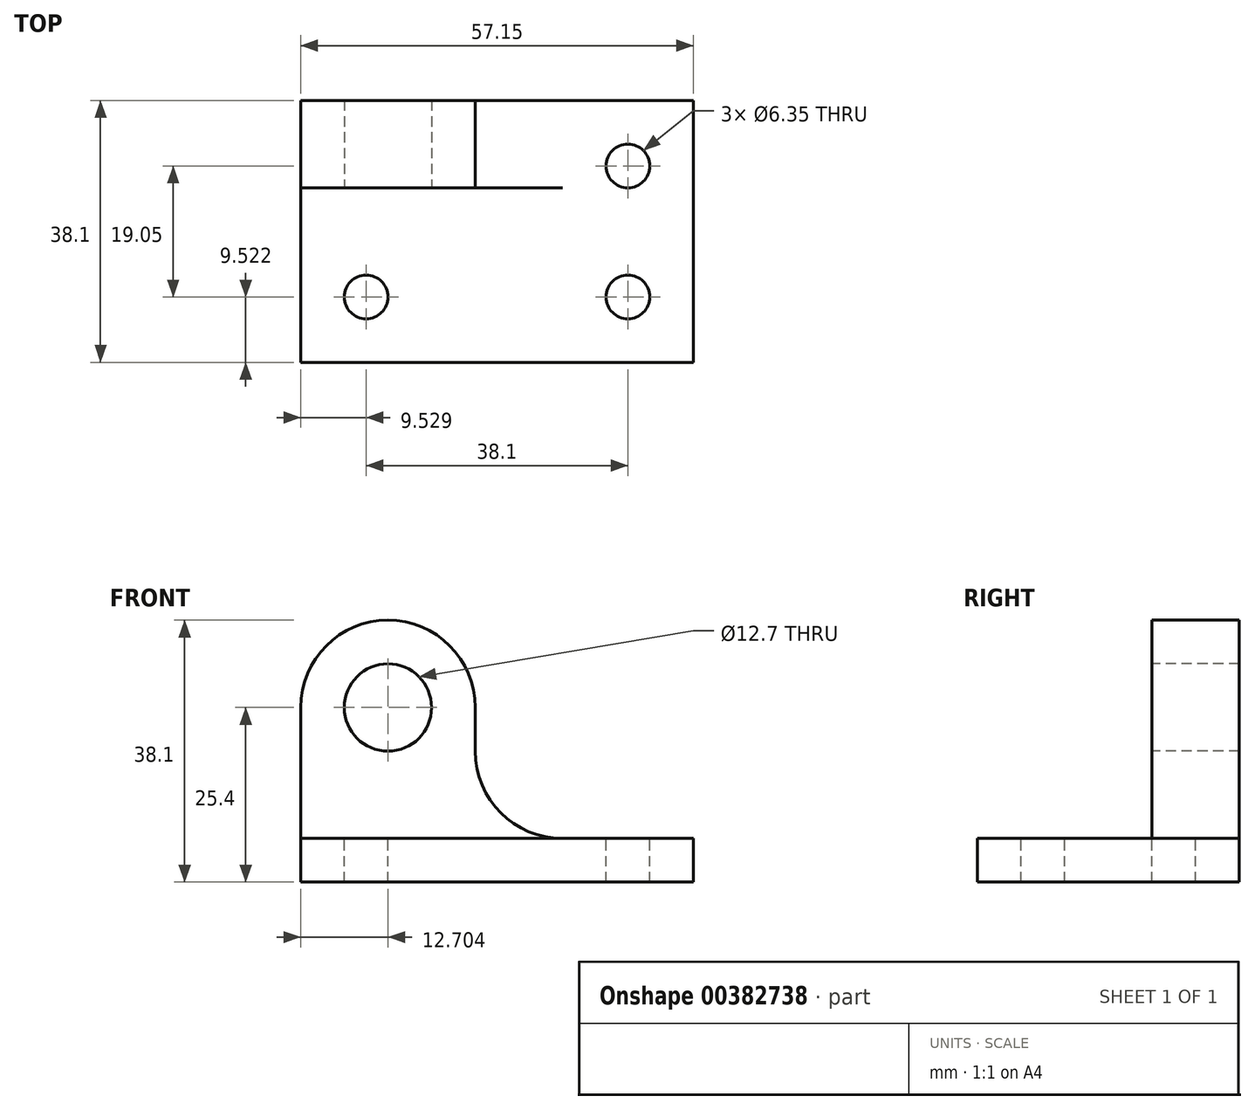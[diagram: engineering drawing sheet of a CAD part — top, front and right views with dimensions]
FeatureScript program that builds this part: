
annotation { "Feature Type Name" : "Feature", "Feature Type Description" : "" }
export const myFeature = defineFeature(function(context is Context, id is Id, definition is map)
    precondition{}
    {
        {
            var Q0;
            Q0=qCreatedBy(makeId("Top.planeOp"),FACE);
            var sketch = newSketch(context, id + "F0", { "sketchPlane" : qUnion([Q0])});
            skLineSegment(sketch, "E0.bottom", {"start": v(-24.7, -21.01) * mm, "end": v(32.44, -21.01) * mm});
            skLineSegment(sketch, "E0.top", {"start": v(-24.7, 17.09) * mm, "end": v(32.44, 17.09) * mm});
            skLineSegment(sketch, "E0.left", {"start": v(-24.7, -21.01) * mm, "end": v(-24.7, 17.09) * mm});
            skLineSegment(sketch, "E0.right", {"start": v(32.44, -21.01) * mm, "end": v(32.44, 17.09) * mm});
            skSolve(sketch);
        }
        {
            var Q0;
            Q0 = qSketchRegion(id + "F0", true);
            extrude(context, id + "F1", {"entities" : qUnion([Q0]), "depth" : 6.35 * mm});
        }
        {
            var Q0;
            Q0=makeQuery(id+"F1.opExtrude","CAP_FACE",FACE,{"disambiguationData":[OSD([sQuery(id+"F0.wireOp",EDGE,"E0.bottom"),sQuery(id+"F0.wireOp",EDGE,"E0.top"),sQuery(id+"F0.wireOp",EDGE,"E0.left"),sQuery(id+"F0.wireOp",EDGE,"E0.right")])],"isStart":false});
            var sketch = newSketch(context, id + "F2", { "sketchPlane" : qUnion([Q0])});
            skLineSegment(sketch, "E1", {"start": v(-24.7, 4.39) * mm, "end": v(0.7, 4.39) * mm});
            skLineSegment(sketch, "E2", {"start": v(0.7, 4.39) * mm, "end": v(0.7, 17.09) * mm});
            skSolve(sketch);
        }
        {
            var Q0;
            {var subQ0=sQuery(id+"F2.wireOp",EDGE,"E1");Q0=makeQuery(id+"F2.imprint","IMPRINT",FACE,{"disambiguationData":[TD([[makeQuery(id+"F2.imprint","IMPRINT",EDGE,{"derivedFrom":subQ0}),1.0]])]});}
            extrude(context, id + "F3", {"entities" : qUnion([Q0]), "operationType" : NewBodyOperationType.ADD, "depth" : 31.75 * mm});
        }
        {
            var Q0;
            Q0=makeQuery(id+"F3.opExtrude","SWEPT_FACE",FACE,{"disambiguationData":[OSD([sQuery(id+"F2.wireOp",EDGE,"E1")])]});
            var sketch = newSketch(context, id + "F4", { "sketchPlane" : qUnion([Q0])});
            skArc(sketch, "E3", {"start": v(0.7, 25.4) * mm, "mid": v(-12, 38.1) * mm, "end": v(-24.7, 25.4) * mm});
            skCircle(sketch, "E4", {"center": v(-12, 25.4) * mm, "radius": 6.35 * mm});
            skLineSegment(sketch, "E5", {"start": v(0.7, 25.4) * mm, "end": v(0.7, 19.05) * mm});
            skArc(sketch, "E6", {"start": v(0.7, 19.05) * mm, "mid": v(4.53, 9.95) * mm, "end": v(13.72, 6.35) * mm});
            skSolve(sketch);
        }
        {
            var Q0;
            {var subQ0=sQuery(id+"F4.wireOp",EDGE,"E3");var subQ1=sQuery(id+"F2.wireOp",EDGE,"E1");var subQ4=makeQuery(id+"F3.opExtrude","CAP_EDGE",EDGE,{"disambiguationData":[OSD([subQ1])],"isStart":false});var subQ5=makeQuery(id+"F4.imprint","INTERSECT",VERTEX,{"derivedFrom":[subQ4,subQ0]});Q0=makeQuery(id+"F4.imprint","IMPRINT",FACE,{"disambiguationData":[TD([[makeQuery(id+"F4.imprint","IMPRINT",EDGE,{"disambiguationData":[TD([[subQ5,-1.0]])],"derivedFrom":subQ0}),-1.0]])]});}
            var Q1;
            {var subQ0=sQuery(id+"F4.wireOp",EDGE,"E3");var subQ1=sQuery(id+"F2.wireOp",EDGE,"E1");var subQ4=makeQuery(id+"F3.opExtrude","CAP_EDGE",EDGE,{"disambiguationData":[OSD([subQ1])],"isStart":false});var subQ5=makeQuery(id+"F4.imprint","INTERSECT",VERTEX,{"derivedFrom":[subQ4,subQ0]});Q1=makeQuery(id+"F4.imprint","IMPRINT",FACE,{"disambiguationData":[TD([[makeQuery(id+"F4.imprint","IMPRINT",EDGE,{"disambiguationData":[TD([[subQ5,-1.0]])],"derivedFrom":subQ4}),-1.0]])]});}
            var Q2;
            Q2=makeQuery(id+"F4.imprint","IMPRINT",FACE,{"disambiguationData":[TD([[makeQuery(id+"F4.imprint","IMPRINT",EDGE,{"derivedFrom":sQuery(id+"F4.wireOp",EDGE,"E4")}),1.0]])]});
            extrude(context, id + "F5", {"entities" : qUnion([Q0, Q1, Q2]), "operationType" : NewBodyOperationType.REMOVE, "oppositeDirection" : true, "depth" : 25.4 * mm});
        }
        {
            var Q0;
            Q0=makeQuery(id+"F1.opExtrude","CAP_FACE",FACE,{"disambiguationData":[OSD([sQuery(id+"F0.wireOp",EDGE,"E0.bottom"),sQuery(id+"F0.wireOp",EDGE,"E0.top"),sQuery(id+"F0.wireOp",EDGE,"E0.left"),sQuery(id+"F0.wireOp",EDGE,"E0.right")])],"isStart":false});
            var sketch = newSketch(context, id + "F6", { "sketchPlane" : qUnion([Q0])});
            skLineSegment(sketch, "E7", {"start": v(0.7, 4.39) * mm, "end": v(13.4, 4.39) * mm});
            skLineSegment(sketch, "E8", {"start": v(13.4, 4.39) * mm, "end": v(13.4, 17.09) * mm});
            skSolve(sketch);
        }
        {
            var Q0;
            Q0=makeQuery(id+"F6.imprint","IMPRINT",FACE,{"disambiguationData":[TD([[makeQuery(id+"F6.imprint","IMPRINT",EDGE,{"derivedFrom":sQuery(id+"F6.wireOp",EDGE,"E7")}),1.0]])]});
            extrude(context, id + "F7", {"entities" : qUnion([Q0]), "operationType" : NewBodyOperationType.ADD, "depth" : 12.7 * mm});
        }
        {
            var Q0;
            Q0=makeQuery(id+"F7.boolean.opBoolean","MERGE",FACE,{"derivedFrom":[makeQuery(id+"F3.opExtrude","SWEPT_FACE",FACE,{"disambiguationData":[OSD([sQuery(id+"F2.wireOp",EDGE,"E1")])]}),makeQuery(id+"F7.opExtrude","SWEPT_FACE",FACE,{"disambiguationData":[OSD([sQuery(id+"F6.wireOp",EDGE,"E7")])]})]});
            var sketch = newSketch(context, id + "F8", { "sketchPlane" : qUnion([Q0])});
            skArc(sketch, "E9", {"start": v(0.7, 19.05) * mm, "mid": v(4.53, 9.96) * mm, "end": v(13.72, 6.35) * mm});
            skSolve(sketch);
        }
        {
            var Q0;
            {var subQ2=sQuery(id+"F6.wireOp",EDGE,"E7");var subQ3=makeQuery(id+"F7.opExtrude","CAP_EDGE",EDGE,{"disambiguationData":[OSD([subQ2])],"isStart":false});Q0=makeQuery(id+"F8.imprint","IMPRINT",FACE,{"disambiguationData":[TD([[makeQuery(id+"F8.imprint","IMPRINT",EDGE,{"derivedFrom":subQ3}),-1.0]])]});}
            extrude(context, id + "F9", {"entities" : qUnion([Q0]), "operationType" : NewBodyOperationType.REMOVE, "oppositeDirection" : true, "depth" : 25.4 * mm});
        }
        {
            var Q0;
            Q0=makeQuery(id+"F1.opExtrude","CAP_FACE",FACE,{"disambiguationData":[OSD([sQuery(id+"F0.wireOp",EDGE,"E0.bottom"),sQuery(id+"F0.wireOp",EDGE,"E0.top"),sQuery(id+"F0.wireOp",EDGE,"E0.left"),sQuery(id+"F0.wireOp",EDGE,"E0.right")])],"isStart":false});
            var sketch = newSketch(context, id + "F10", { "sketchPlane" : qUnion([Q0])});
            skCircle(sketch, "E10", {"center": v(22.92, 7.56) * mm, "radius": 3.18 * mm});
            skCircle(sketch, "E11", {"center": v(-15.18, -11.49) * mm, "radius": 3.18 * mm});
            skCircle(sketch, "E12", {"center": v(22.92, -11.49) * mm, "radius": 3.18 * mm});
            skSolve(sketch);
        }
        {
            var Q0;
            Q0=makeQuery(id+"F10.imprint","IMPRINT",FACE,{"disambiguationData":[TD([[makeQuery(id+"F10.imprint","IMPRINT",EDGE,{"derivedFrom":sQuery(id+"F10.wireOp",EDGE,"E11")}),1.0]])]});
            var Q1;
            Q1=makeQuery(id+"F10.imprint","IMPRINT",FACE,{"disambiguationData":[TD([[makeQuery(id+"F10.imprint","IMPRINT",EDGE,{"derivedFrom":sQuery(id+"F10.wireOp",EDGE,"E12")}),1.0]])]});
            var Q2;
            Q2=makeQuery(id+"F10.imprint","IMPRINT",FACE,{"disambiguationData":[TD([[makeQuery(id+"F10.imprint","IMPRINT",EDGE,{"derivedFrom":sQuery(id+"F10.wireOp",EDGE,"E10")}),1.0]])]});
            extrude(context, id + "F11", {"entities" : qUnion([Q0, Q1, Q2]), "operationType" : NewBodyOperationType.REMOVE, "oppositeDirection" : true, "depth" : 25.4 * mm});
        }
    });
